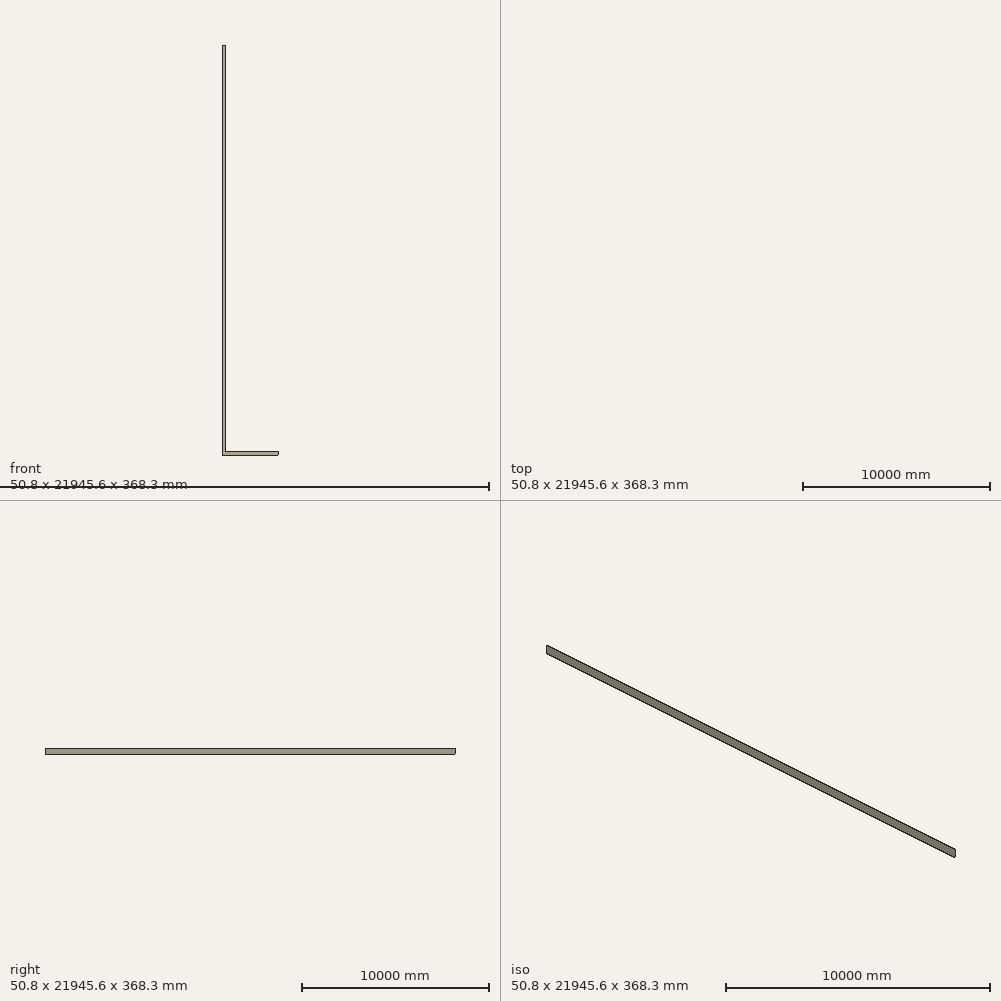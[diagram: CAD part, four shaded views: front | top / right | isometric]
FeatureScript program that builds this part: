
annotation { "Feature Type Name" : "Feature", "Feature Type Description" : "" }
export const myFeature = defineFeature(function(context is Context, id is Id, definition is map)
    precondition{}
    {
        {
            var Q0;
            Q0=qCreatedBy(makeId("Front.planeOp"),FACE);
            var sketch = newSketch(context, id + "F0", { "sketchPlane" : qUnion([Q0])});
            skLineSegment(sketch, "E0", {"start": v(0, 0) * mm, "end": v(0, 368.3) * mm});
            skLineSegment(sketch, "E1", {"start": v(0, 0) * mm, "end": v(50.8, 0) * mm});
            skLineSegment(sketch, "E2", {"start": v(50.8, 0) * mm, "end": v(50.8, 3.18) * mm});
            skLineSegment(sketch, "E3", {"start": v(50.8, 3.18) * mm, "end": v(3.17, 3.18) * mm});
            skLineSegment(sketch, "E4", {"start": v(3.17, 3.17) * mm, "end": v(3.17, 368.3) * mm});
            skLineSegment(sketch, "E5", {"start": v(3.17, 368.3) * mm, "end": v(0, 368.3) * mm});
            skSolve(sketch);
        }
        {
            var Q0;
            Q0=makeQuery(id+"F0.imprint","IMPRINT",FACE,{"disambiguationData":[TD([[makeQuery(id+"F0.imprint","IMPRINT",EDGE,{"derivedFrom":sQuery(id+"F0.wireOp",EDGE,"E0")}),-1.0]])]});
            extrude(context, id + "F1", {"entities" : qUnion([Q0]), "oppositeDirection" : true, "depth" : 21945.6 * mm, "offsetDistance" : 25.4 * mm});
        }
    });
